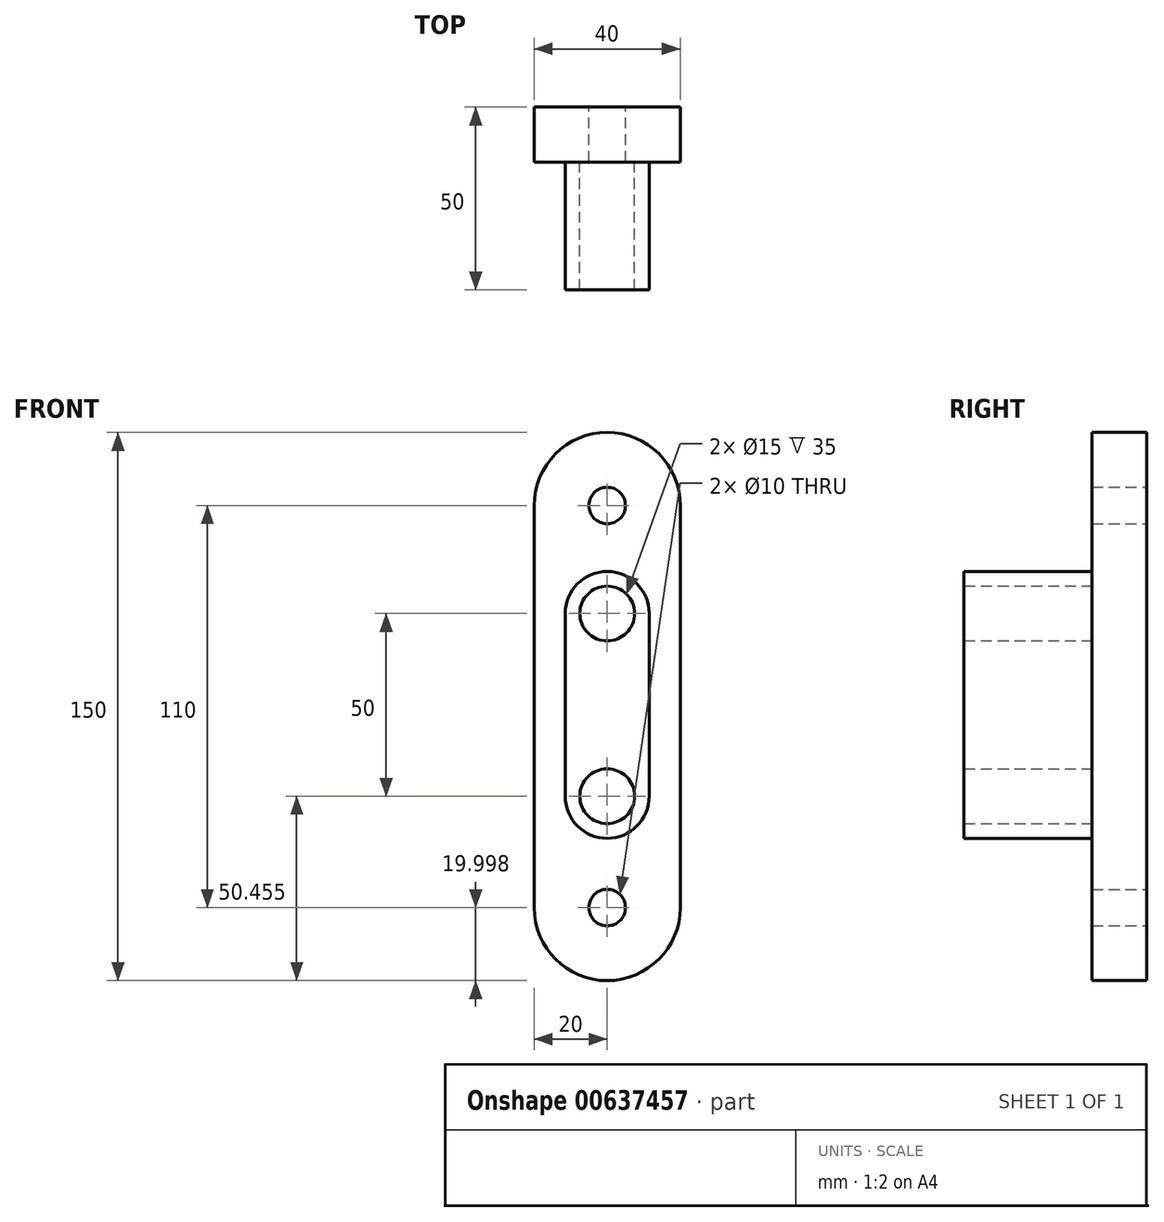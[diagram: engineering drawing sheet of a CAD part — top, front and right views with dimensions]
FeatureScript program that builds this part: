
annotation { "Feature Type Name" : "Feature", "Feature Type Description" : "" }
export const myFeature = defineFeature(function(context is Context, id is Id, definition is map)
    precondition{}
    {
        {
            var Q0;
            Q0=qCreatedBy(makeId("Front.planeOp"),FACE);
            var sketch = newSketch(context, id + "F0", { "sketchPlane" : qUnion([Q0])});
            skCircle(sketch, "E0", {"center": v(0, 26.23) * mm, "radius": 7.5 * mm});
            skArc(sketch, "E1", {"start": v(11.5, 26.23) * mm, "mid": v(0, 37.73) * mm, "end": v(-11.5, 26.23) * mm});
            skCircle(sketch, "E2", {"center": v(0, -23.77) * mm, "radius": 7.5 * mm});
            skArc(sketch, "E3", {"start": v(-11.5, -23.77) * mm, "mid": v(0, -35.27) * mm, "end": v(11.5, -23.77) * mm});
            skLineSegment(sketch, "E4", {"start": v(-11.5, 26.23) * mm, "end": v(-11.5, -23.77) * mm});
            skLineSegment(sketch, "E5", {"start": v(11.5, -23.77) * mm, "end": v(11.5, 26.23) * mm});
            skSolve(sketch);
        }
        {
            var Q0;
            Q0 = qSketchRegion(id + "F0", true);
            extrude(context, id + "F1", {"entities" : qUnion([Q0]), "depth" : 50 * mm, "offsetDistance" : 25 * mm});
        }
        {
            var Q0;
            Q0=qCreatedBy(makeId("Front.planeOp"),FACE);
            var sketch = newSketch(context, id + "F2", { "sketchPlane" : qUnion([Q0])});
            skArc(sketch, "E6", {"start": v(-20, -54.22) * mm, "mid": v(0, -74.22) * mm, "end": v(20, -54.22) * mm});
            skArc(sketch, "E7", {"start": v(20, 55.78) * mm, "mid": v(0, 75.78) * mm, "end": v(-20, 55.78) * mm});
            skLineSegment(sketch, "E8", {"start": v(-20, 55.78) * mm, "end": v(-20, -54.22) * mm});
            skLineSegment(sketch, "E9", {"start": v(20, -54.22) * mm, "end": v(20, 55.78) * mm});
            skCircle(sketch, "E10", {"center": v(0, -54.22) * mm, "radius": 5 * mm});
            skCircle(sketch, "E11", {"center": v(0, 55.78) * mm, "radius": 5 * mm});
            skSolve(sketch);
        }
        {
            var Q0;
            Q0 = qSketchRegion(id + "F2", true);
            extrude(context, id + "F3", {"entities" : qUnion([Q0]), "operationType" : NewBodyOperationType.ADD, "depth" : 15 * mm, "offsetDistance" : 25 * mm});
        }
    });
